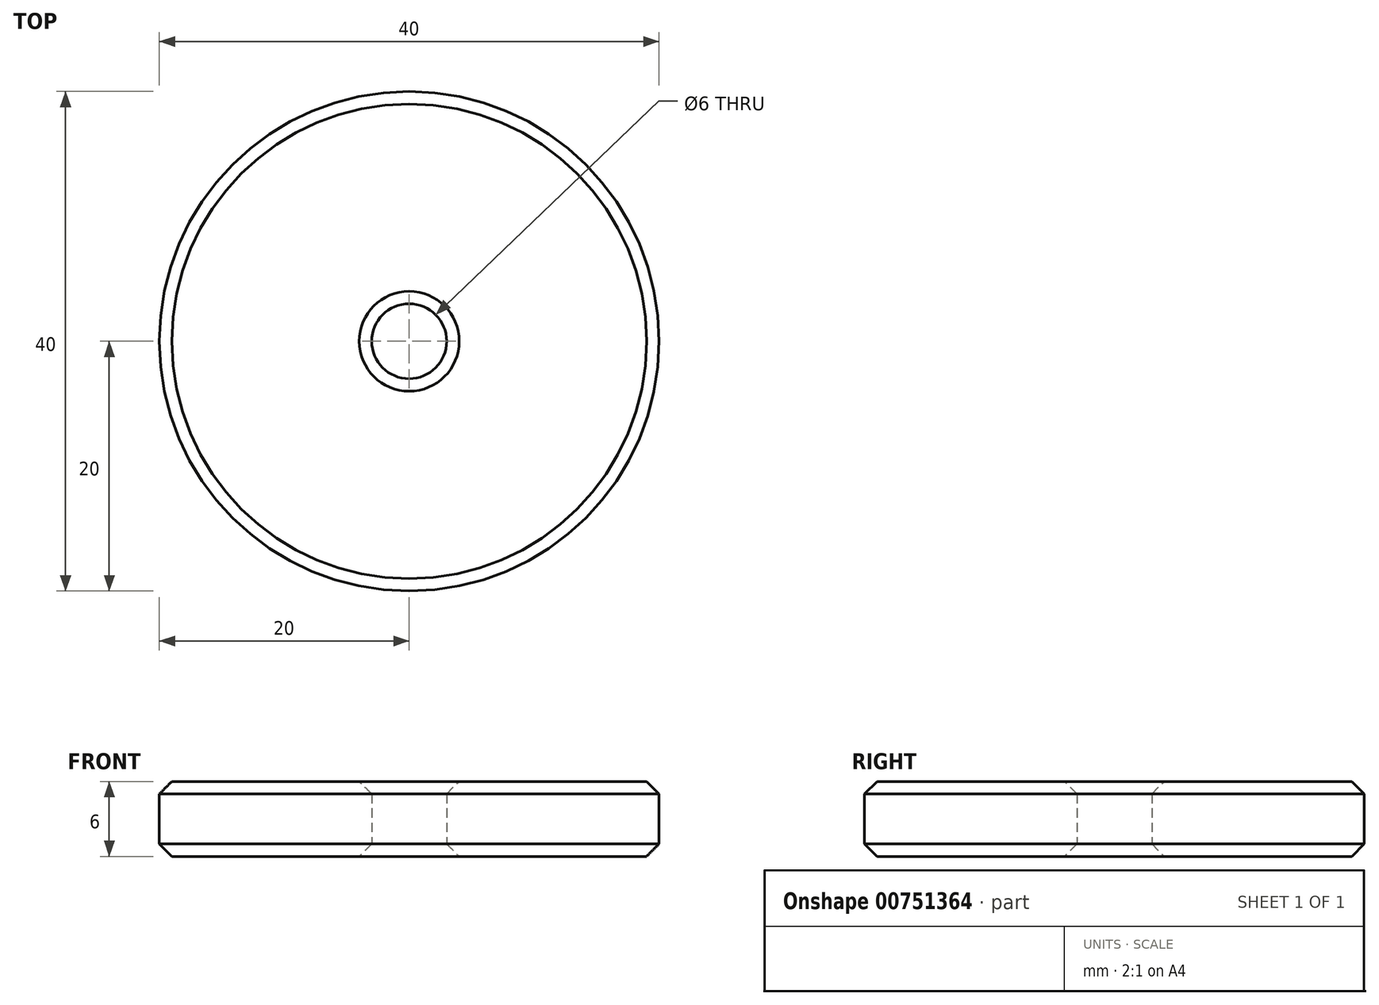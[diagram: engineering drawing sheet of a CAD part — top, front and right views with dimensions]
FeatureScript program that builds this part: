
annotation { "Feature Type Name" : "Feature", "Feature Type Description" : "" }
export const myFeature = defineFeature(function(context is Context, id is Id, definition is map)
    precondition{}
    {
        {
            var Q0;
            Q0=qCreatedBy(makeId("Front.planeOp"),FACE);
            var sketch = newSketch(context, id + "F0", { "sketchPlane" : qUnion([Q0])});
            skLineSegment(sketch, "E0", {"start": v(-3, 0) * mm, "end": v(-3, 6) * mm});
            skLineSegment(sketch, "E1", {"start": v(-3, 6) * mm, "end": v(-20, 6) * mm});
            skLineSegment(sketch, "E2", {"start": v(-20, 6) * mm, "end": v(-20, 0) * mm});
            skLineSegment(sketch, "E3", {"start": v(-20, 0) * mm, "end": v(-3, 0) * mm});
            skLineSegment(sketch, "E4", {"start": v(0, 0) * mm, "end": v(-3, 0) * mm, "construction": true});
            skLineSegment(sketch, "E5", {"start": v(0, 0) * mm, "end": v(0, 9.56) * mm, "construction": true});
            skLineSegment(sketch, "E6", {"start": v(-3, 6) * mm, "end": v(6.25, 6) * mm, "construction": true});
            skSolve(sketch);
        }
        {
            var Q0;
            Q0 = qSketchRegion(id + "F0", true);
            var Q1;
            Q1=sQuery(id+"F0.wireOp",EDGE,"E5");
            revolve(context, id + "F1", {"surfaceOperationType" : NewSurfaceOperationType.NEW, "entities" : qUnion([Q0]), "axis" : qUnion([Q1]), "revolveType" : RevolveType.FULL});
        }
        {
            var Q0;
            Q0=makeQuery(id+"F1.opRevolve","SWEPT_EDGE",EDGE,{"disambiguationData":[OSD([sQuery(id+"F0.wireOp",EDGE,"E1"),sQuery(id+"F0.wireOp",EDGE,"E2")])]});
            var Q1;
            Q1=makeQuery(id+"F1.opRevolve","SWEPT_EDGE",EDGE,{"disambiguationData":[OSD([sQuery(id+"F0.wireOp",EDGE,"E2"),sQuery(id+"F0.wireOp",EDGE,"E3")])]});
            var Q2;
            Q2=makeQuery(id+"F1.opRevolve","SWEPT_EDGE",EDGE,{"disambiguationData":[OSD([sQuery(id+"F0.wireOp",EDGE,"E0"),sQuery(id+"F0.wireOp",EDGE,"E1")])]});
            var Q3;
            Q3=makeQuery(id+"F1.opRevolve","SWEPT_EDGE",EDGE,{"disambiguationData":[OSD([sQuery(id+"F0.wireOp",EDGE,"E0"),sQuery(id+"F0.wireOp",EDGE,"E3")])]});
            chamfer(context, id + "F2", {"entities" : qUnion([Q0, Q1, Q2, Q3]), "width" : 1 * mm, "tangentPropagation" : true});
        }
    });
